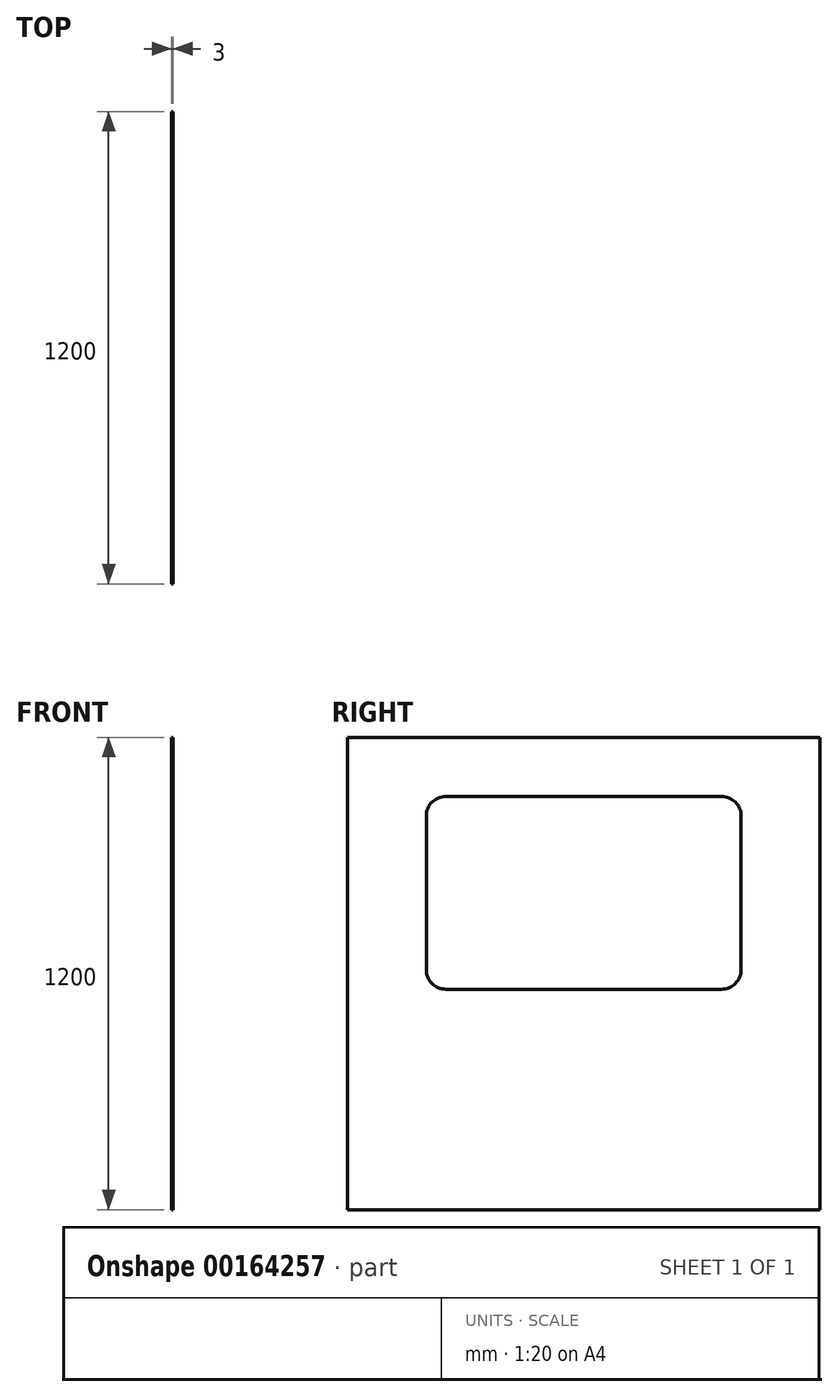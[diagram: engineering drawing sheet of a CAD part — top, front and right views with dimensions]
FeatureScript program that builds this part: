
annotation { "Feature Type Name" : "Feature", "Feature Type Description" : "" }
export const myFeature = defineFeature(function(context is Context, id is Id, definition is map)
    precondition{}
    {
        {
            var Q0;
            Q0=qCreatedBy(makeId("Right.planeOp"),FACE);
            var sketch = newSketch(context, id + "F0", { "sketchPlane" : qUnion([Q0])});
            skLineSegment(sketch, "E0.bottom", {"start": v(-965.5, 610.14) * mm, "end": v(234.5, 610.14) * mm});
            skLineSegment(sketch, "E0.top", {"start": v(-965.5, -589.86) * mm, "end": v(234.5, -589.86) * mm});
            skLineSegment(sketch, "E0.left", {"start": v(-965.5, 610.14) * mm, "end": v(-965.5, -589.86) * mm});
            skLineSegment(sketch, "E0.right", {"start": v(234.5, 610.14) * mm, "end": v(234.5, -589.86) * mm});
            skLineSegment(sketch, "E1.bottom", {"start": v(-715.5, 460.14) * mm, "end": v(-15.5, 460.14) * mm});
            skLineSegment(sketch, "E1.top", {"start": v(-715.5, -29.86) * mm, "end": v(-15.5, -29.86) * mm});
            skLineSegment(sketch, "E1.left", {"start": v(-765.5, 410.14) * mm, "end": v(-765.5, 20.14) * mm});
            skLineSegment(sketch, "E1.right", {"start": v(34.5, 410.14) * mm, "end": v(34.5, 20.14) * mm});
            skPoint(sketch, "E2.visualSharp", {"position": v(-765.5, 460.14) * mm});
            skArc(sketch, "E2.filletArc", {"start": v(-715.5, 460.14) * mm, "mid": v(-750.86, 445.5) * mm, "end": v(-765.5, 410.14) * mm});
            skPoint(sketch, "E3.visualSharp", {"position": v(-765.5, -29.86) * mm});
            skArc(sketch, "E3.filletArc", {"start": v(-765.5, 20.14) * mm, "mid": v(-750.86, -15.21) * mm, "end": v(-715.5, -29.86) * mm});
            skPoint(sketch, "E4.visualSharp", {"position": v(34.5, -29.86) * mm});
            skArc(sketch, "E4.filletArc", {"start": v(-15.5, -29.86) * mm, "mid": v(19.85, -15.21) * mm, "end": v(34.5, 20.14) * mm});
            skPoint(sketch, "E5.visualSharp", {"position": v(34.5, 460.14) * mm});
            skArc(sketch, "E5.filletArc", {"start": v(34.5, 410.14) * mm, "mid": v(19.85, 445.5) * mm, "end": v(-15.5, 460.14) * mm});
            skSolve(sketch);
        }
        {
            var Q0;
            Q0 = qSketchRegion(id + "F0", true);
            extrude(context, id + "F1", {"entities" : qUnion([Q0]), "oppositeDirection" : true, "depth" : 3 * mm});
        }
    });
